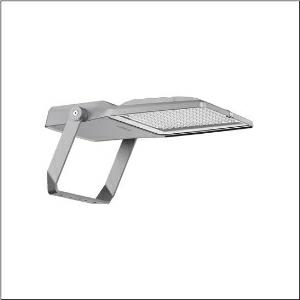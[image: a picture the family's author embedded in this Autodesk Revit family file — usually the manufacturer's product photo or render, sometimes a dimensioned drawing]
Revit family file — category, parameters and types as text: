
# Revit family: floodlight_fl_21_midi___pl61_5xa7786e4c1a_1b6e
name_source: partatom
category: Lighting Fixtures
units: mm (PartAtom-declared; Revit-internal decimal feet)

## family parameters
Cut with Voids When Loaded = No
Host = Face
Light Source = No
Part Type = Normal
Room Calculation Point = No
Round Connector Dimension = Use Diameter
Shared = No

## types (1)
- --- (1 x LED, 27590 lm, 212.4 W, 4000K)
    Apparent Load = 212 VA
    CIE Flux Codes = 33 65 98 100 100
    Color Rendering = 70
    Color Temperature = 4000K
    Default Elevation = 1800 mm
    Description = Floodlight FL 21 midi, floodlight, primary light control with lens, of PMMA, primary optical cover: protective disc, of toughened safety glass, transparent, light distribution: PL61, light emission: direct distribution, installation type: surface-mounted, LED, High Power LED, rated luminous flux: 27.590lm, luminous efficacy: 130lm/W, light colour: 740, colour temperature: 4000K, control gear: Smart Interface (Zhaga)D4i, control: overheat protection, constant luminous flux control, time-dependent luminous flux control, flexible luminous flux parameterisation, pre-setting: logarithmic dimming characteristic, with terminal, 6-pole, mains connection: 220..240V, AC, 50/60Hz, start of lifetime: 212W, end of service life: 231W, reduction: 95W, mounting bracket, of diecast aluminium, powder-coated, SITECO metallic grey (DB 702S), corrosivity category C5 mid according to DIN EN ISO 12944, suitable for swimming pools, chlorine-resistant, sealing non-destructively replaceable, mounting bracket, of steel, galvanised, powder-coated, SITECO metallic grey (DB 702S), Smart Interface below and above, protection rating (complete): IP66, insulation class (complete): insulation class II (safety insulation), certification: CE, ENEC, VDE, protection symbol: D, impact resistance: IK08, permissible operating ambient temperature: -40..+40°C, permissible operating ambient temperature for outdoor applications: -40..+50°C, standard: DIN EN 12944, LABS conformity tested according to VDMA 24364:2018-05, packaging unit: 1 piece

Light Distribution: PL61
    Height = 76 mm
    Lamp = 1 x LED
    Lamp Light Flux = 27590 lm
    Lamp Power = 212.4 W
    Lamp count = 1
    Length = 657 mm
    Luminous efficacy = 130 lm/W
    Manufacturer = Siteco
    ModVariant = No
    Model = 5XA7786E4C1A
    Number of Poles = 1
    OnlyDefault = Yes
    Power Factor = 1
    Product Name = Floodlight FL 21 midi | PL61
    Product group = floodlight | pylon annexe
    ProductGroupID = 6201
    Protection Class = Protection class II
    Protection Degree = IP 66
    RLX_Detail_Level = 1
    RLX_Emergency_Light_Flux = 0 lm
    RLX_Emergency_Type = 0
    RLX_Emergency_Type_DB = No
    RlxData = <blob elided: 101701 chars, md5=f99fea2e>
    Socket = socket
    Standby Power = 0 W
    System Light Flux = 27590 lm
    System Power = 212 W
    Type Comments = factory setting: luminous flux: 100 % | dim-lin: 254 | 710 mA
    Type Image = l_1006876.jpg
    URL = http://relux.com
    VarID = @adj_094397
    Voltage = 0 V
    Weight = 0.00 kg
    Width = 442 mm

## geometry (parser evidence)
native form markers: Blend x4, Sweep x13
no freeform markers — native parametric forms only
